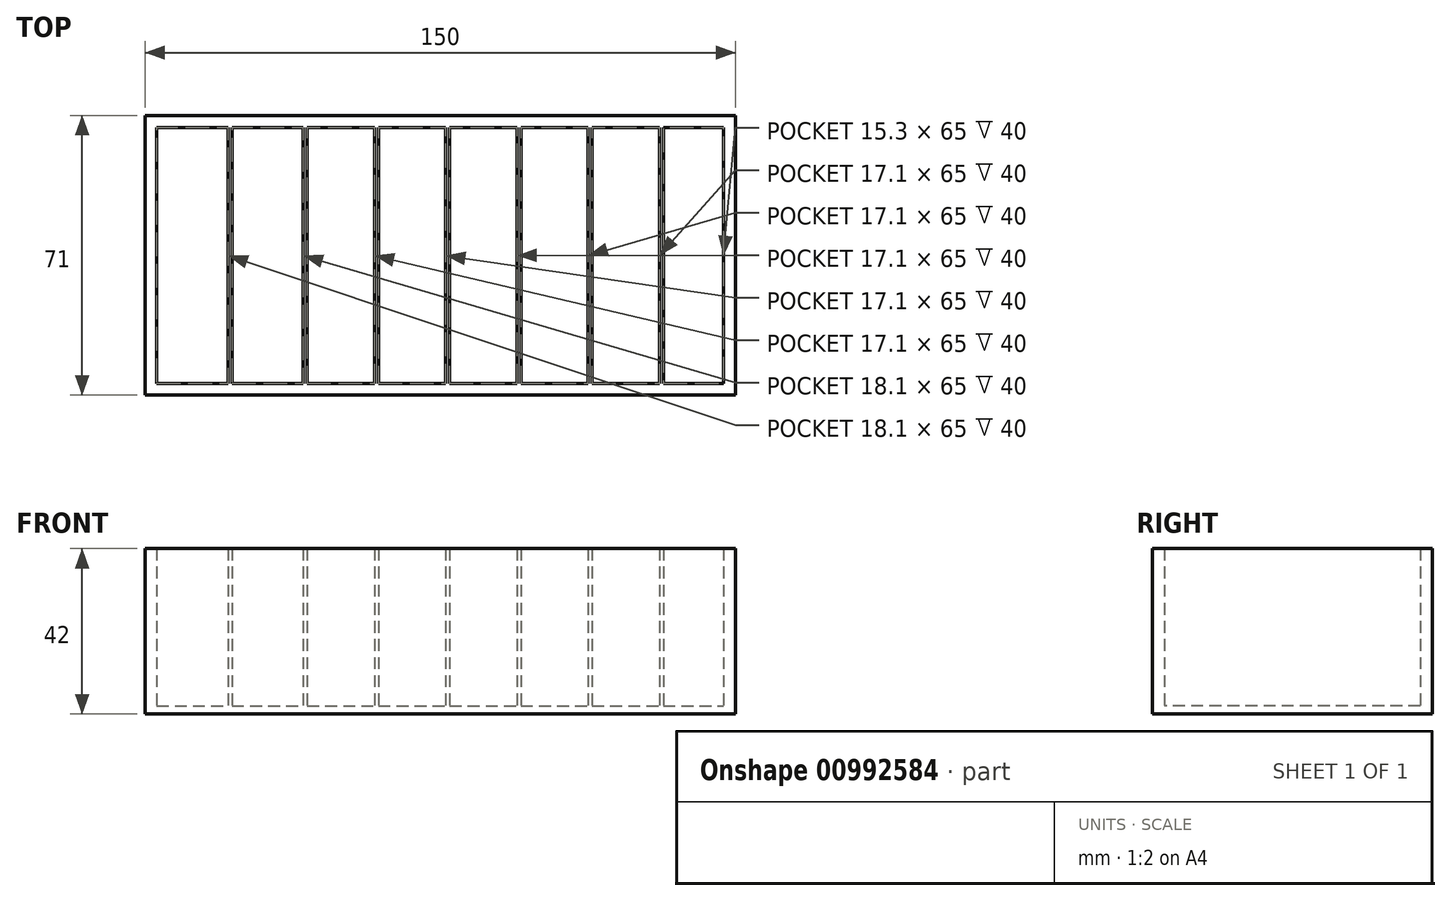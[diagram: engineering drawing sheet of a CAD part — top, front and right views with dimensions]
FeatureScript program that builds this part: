
annotation { "Feature Type Name" : "Feature", "Feature Type Description" : "" }
export const myFeature = defineFeature(function(context is Context, id is Id, definition is map)
    precondition{}
    {
        {
            var Q0;
            Q0=qCreatedBy(makeId("Top.planeOp"),FACE);
            var sketch = newSketch(context, id + "F0", { "sketchPlane" : qUnion([Q0])});
            skLineSegment(sketch, "E0.bottom", {"start": v(0, 0) * mm, "end": v(150, 0) * mm});
            skLineSegment(sketch, "E0.top", {"start": v(0, 71) * mm, "end": v(150, 71) * mm});
            skLineSegment(sketch, "E0.left", {"start": v(0, 0) * mm, "end": v(0, 71) * mm});
            skLineSegment(sketch, "E0.right", {"start": v(150, 0) * mm, "end": v(150, 71) * mm});
            skSolve(sketch);
        }
        {
            var Q0;
            Q0=makeQuery(id+"F0.imprint","IMPRINT",FACE,{"disambiguationData":[TD([[makeQuery(id+"F0.imprint","IMPRINT",EDGE,{"derivedFrom":sQuery(id+"F0.wireOp",EDGE,"E0.bottom")}),1.0]])]});
            extrude(context, id + "F1", {"entities" : qUnion([Q0]), "depth" : 2 * mm, "offsetDistance" : 25 * mm});
        }
        {
            var Q0;
            Q0=makeQuery(id+"F1.opExtrude","CAP_FACE",FACE,{"disambiguationData":[OSD([sQuery(id+"F0.wireOp",EDGE,"E0.bottom"),sQuery(id+"F0.wireOp",EDGE,"E0.top"),sQuery(id+"F0.wireOp",EDGE,"E0.left"),sQuery(id+"F0.wireOp",EDGE,"E0.right")])],"isStart":false});
            var sketch = newSketch(context, id + "F2", { "sketchPlane" : qUnion([Q0])});
            skLineSegment(sketch, "E1.bottom", {"start": v(3, 3) * mm, "end": v(147, 3) * mm});
            skLineSegment(sketch, "E1.top", {"start": v(3, 68) * mm, "end": v(147, 68) * mm});
            skLineSegment(sketch, "E1.left", {"start": v(3, 3) * mm, "end": v(3, 68) * mm});
            skLineSegment(sketch, "E1.right", {"start": v(147, 3) * mm, "end": v(147, 68) * mm});
            skSolve(sketch);
        }
        {
            var Q0;
            Q0=makeQuery(id+"F2.imprint","IMPRINT",FACE,{"disambiguationData":[TD([[makeQuery(id+"F2.imprint","IMPRINT",EDGE,{"derivedFrom":sQuery(id+"F2.wireOp",EDGE,"E1.bottom")}),-1.0]])]});
            extrude(context, id + "F3", {"entities" : qUnion([Q0]), "operationType" : NewBodyOperationType.ADD, "depth" : 40 * mm, "offsetDistance" : 25 * mm});
        }
        {
            var Q0;
            Q0=makeQuery(id+"F1.opExtrude","CAP_FACE",FACE,{"disambiguationData":[OSD([sQuery(id+"F0.wireOp",EDGE,"E0.bottom"),sQuery(id+"F0.wireOp",EDGE,"E0.top"),sQuery(id+"F0.wireOp",EDGE,"E0.left"),sQuery(id+"F0.wireOp",EDGE,"E0.right")])],"isStart":false});
            var sketch = newSketch(context, id + "F4", { "sketchPlane" : qUnion([Q0])});
            skLineSegment(sketch, "E2.bottom", {"start": v(21.1, 68) * mm, "end": v(22.1, 68) * mm});
            skLineSegment(sketch, "E2.top", {"start": v(21.1, 3) * mm, "end": v(22.1, 3) * mm});
            skLineSegment(sketch, "E2.left", {"start": v(21.1, 68) * mm, "end": v(21.1, 3) * mm});
            skLineSegment(sketch, "E2.right", {"start": v(22.1, 68) * mm, "end": v(22.1, 3) * mm});
            skSolve(sketch);
        }
        {
            var Q0;
            Q0=makeQuery(id+"F4.imprint","IMPRINT",FACE,{"disambiguationData":[TD([[makeQuery(id+"F4.imprint","IMPRINT",EDGE,{"derivedFrom":sQuery(id+"F4.wireOp",EDGE,"E2.bottom")}),-1.0]])]});
            extrude(context, id + "F5", {"entities" : qUnion([Q0]), "operationType" : NewBodyOperationType.ADD, "depth" : 40 * mm, "offsetDistance" : 25 * mm});
        }
        {
            var Q0;
            Q0=makeQuery(id+"F5.boolean.opBoolean","SPLIT",FACE,{"disambiguationData":[TD([makeQuery(id+"F3.opExtrude","SWEPT_FACE",FACE,{"disambiguationData":[OSD([sQuery(id+"F2.wireOp",EDGE,"E1.right")])]})])],"derivedFrom":makeQuery(id+"F1.opExtrude","CAP_FACE",FACE,{"disambiguationData":[OSD([sQuery(id+"F0.wireOp",EDGE,"E0.bottom"),sQuery(id+"F0.wireOp",EDGE,"E0.top"),sQuery(id+"F0.wireOp",EDGE,"E0.left"),sQuery(id+"F0.wireOp",EDGE,"E0.right")])],"isStart":false})});
            var sketch = newSketch(context, id + "F6", { "sketchPlane" : qUnion([Q0])});
            skLineSegment(sketch, "E3.bottom", {"start": v(40.2, 68) * mm, "end": v(41.2, 68) * mm});
            skLineSegment(sketch, "E3.top", {"start": v(40.2, 3) * mm, "end": v(41.2, 3) * mm});
            skLineSegment(sketch, "E3.left", {"start": v(40.2, 68) * mm, "end": v(40.2, 3) * mm});
            skLineSegment(sketch, "E3.right", {"start": v(41.2, 68) * mm, "end": v(41.2, 3) * mm});
            skLineSegment(sketch, "E4.1.0.0", {"start": v(59.3, 68) * mm, "end": v(59.3, 3) * mm});
            skLineSegment(sketch, "E4.1.0.1", {"start": v(58.3, 68) * mm, "end": v(58.3, 3) * mm});
            skLineSegment(sketch, "E4.2.0.0", {"start": v(77.4, 68) * mm, "end": v(77.4, 3) * mm});
            skLineSegment(sketch, "E4.2.0.1", {"start": v(76.4, 68) * mm, "end": v(76.4, 3) * mm});
            skLineSegment(sketch, "E4.3.0.0", {"start": v(95.5, 68) * mm, "end": v(95.5, 3) * mm});
            skLineSegment(sketch, "E4.3.0.1", {"start": v(94.5, 68) * mm, "end": v(94.5, 3) * mm});
            skLineSegment(sketch, "E4.4.0.0", {"start": v(113.6, 68) * mm, "end": v(113.6, 3) * mm});
            skLineSegment(sketch, "E4.4.0.1", {"start": v(112.6, 68) * mm, "end": v(112.6, 3) * mm});
            skLineSegment(sketch, "E4.5.0.0", {"start": v(131.7, 68) * mm, "end": v(131.7, 3) * mm});
            skLineSegment(sketch, "E4.5.0.1", {"start": v(130.7, 68) * mm, "end": v(130.7, 3) * mm});
            skLineSegment(sketch, "E4.direction1", {"start": v(41.2, 3) * mm, "end": v(59.3, 3) * mm, "construction": true});
            skSolve(sketch);
        }
        {
            var Q0;
            Q0=makeQuery(id+"F6.imprint","IMPRINT",FACE,{"disambiguationData":[TD([[makeQuery(id+"F6.imprint","IMPRINT",EDGE,{"derivedFrom":sQuery(id+"F6.wireOp",EDGE,"E3.bottom")}),-1.0]])]});
            var Q1;
            {var subQ0=sQuery(id+"F6.wireOp",EDGE,"E4.1.0.0");Q1=makeQuery(id+"F6.imprint","IMPRINT",FACE,{"disambiguationData":[TD([[makeQuery(id+"F6.imprint","IMPRINT",EDGE,{"derivedFrom":subQ0}),-1.0]])]});}
            var Q2;
            {var subQ0=sQuery(id+"F6.wireOp",EDGE,"E4.2.0.0");Q2=makeQuery(id+"F6.imprint","IMPRINT",FACE,{"disambiguationData":[TD([[makeQuery(id+"F6.imprint","IMPRINT",EDGE,{"derivedFrom":subQ0}),-1.0]])]});}
            var Q3;
            {var subQ0=sQuery(id+"F6.wireOp",EDGE,"E4.3.0.0");Q3=makeQuery(id+"F6.imprint","IMPRINT",FACE,{"disambiguationData":[TD([[makeQuery(id+"F6.imprint","IMPRINT",EDGE,{"derivedFrom":subQ0}),-1.0]])]});}
            var Q4;
            {var subQ0=sQuery(id+"F6.wireOp",EDGE,"E4.4.0.0");Q4=makeQuery(id+"F6.imprint","IMPRINT",FACE,{"disambiguationData":[TD([[makeQuery(id+"F6.imprint","IMPRINT",EDGE,{"derivedFrom":subQ0}),-1.0]])]});}
            var Q5;
            {var subQ0=sQuery(id+"F6.wireOp",EDGE,"E4.5.0.0");Q5=makeQuery(id+"F6.imprint","IMPRINT",FACE,{"disambiguationData":[TD([[makeQuery(id+"F6.imprint","IMPRINT",EDGE,{"derivedFrom":subQ0}),-1.0]])]});}
            extrude(context, id + "F7", {"entities" : qUnion([Q0, Q1, Q2, Q3, Q4, Q5]), "operationType" : NewBodyOperationType.ADD, "depth" : 40 * mm, "offsetDistance" : 25 * mm});
        }
    });
